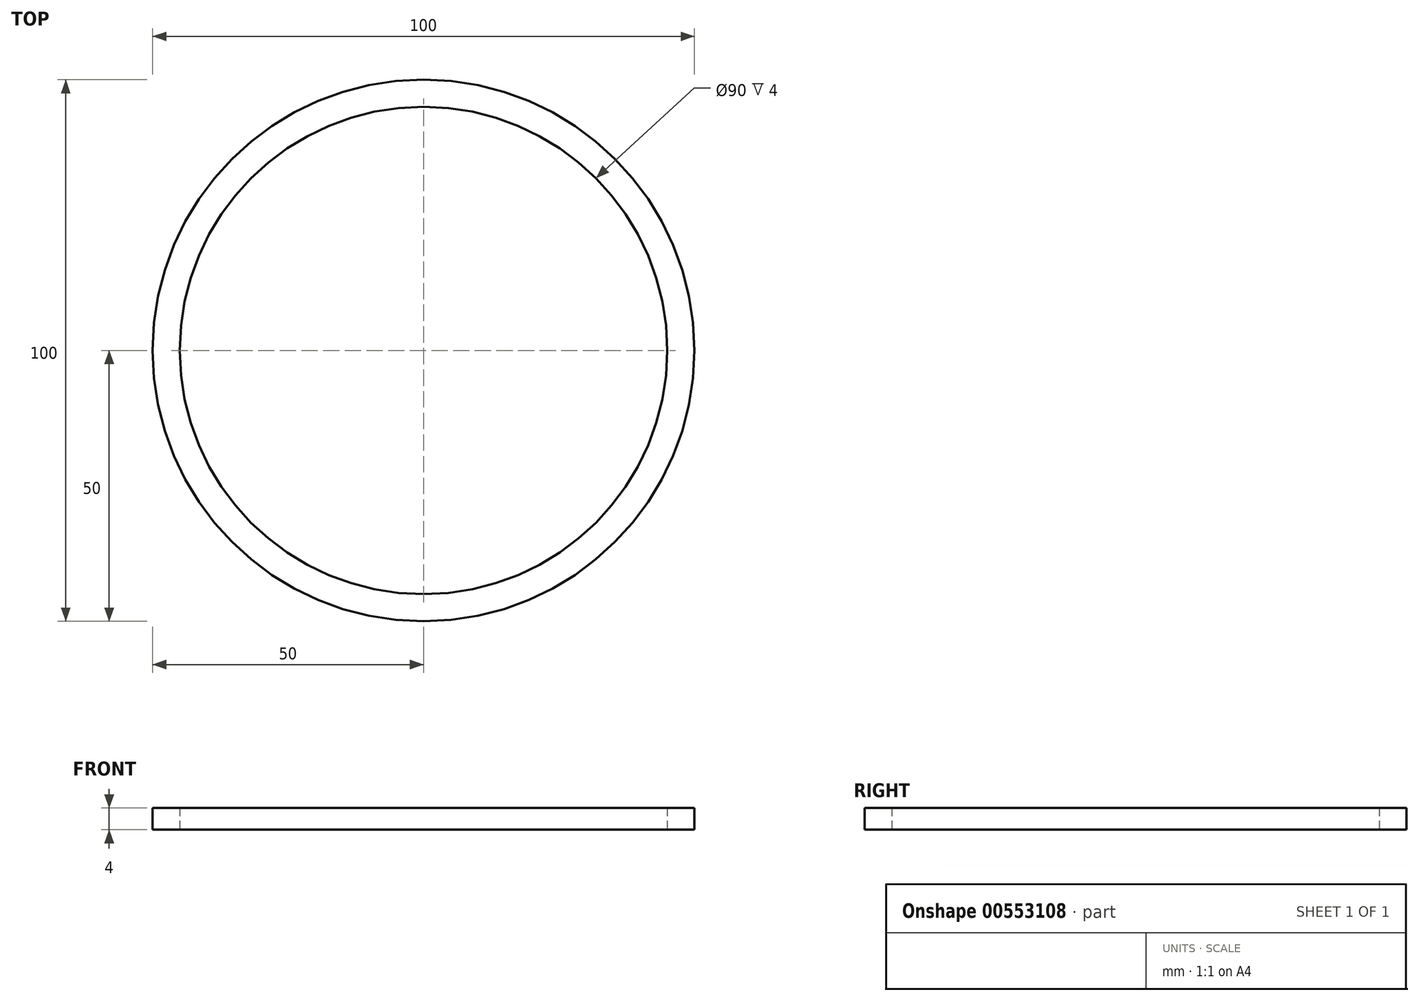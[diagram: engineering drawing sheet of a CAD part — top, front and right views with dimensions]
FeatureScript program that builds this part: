
annotation { "Feature Type Name" : "Feature", "Feature Type Description" : "" }
export const myFeature = defineFeature(function(context is Context, id is Id, definition is map)
    precondition{}
    {
        {
            var Q0;
            Q0=qCreatedBy(makeId("Top.planeOp"),FACE);
            var sketch = newSketch(context, id + "F0", { "sketchPlane" : qUnion([Q0])});
            skCircle(sketch, "E0", {"center": v(0, 0) * mm, "radius": 45 * mm});
            skCircle(sketch, "E1", {"center": v(0, 0) * mm, "radius": 50 * mm});
            skSolve(sketch);
        }
        {
            var Q0;
            Q0=makeQuery(id+"F0.imprint","IMPRINT",FACE,{"disambiguationData":[TD([[makeQuery(id+"F0.imprint","IMPRINT",EDGE,{"derivedFrom":sQuery(id+"F0.wireOp",EDGE,"E0")}),-1.0]])]});
            extrude(context, id + "F1", {"entities" : qUnion([Q0]), "depth" : 4 * mm, "offsetDistance" : 25.4 * mm});
        }
    });
